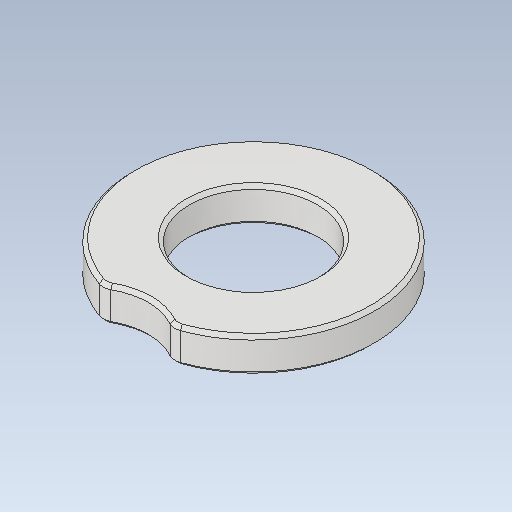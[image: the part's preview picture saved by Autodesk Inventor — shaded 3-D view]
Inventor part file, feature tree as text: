
AUTODESK INVENTOR PART (.ipt)
format: ipt  version: 2020.1 (Build 241239000, 239)  size: 160,256 bytes
history: native  units: mm
features: chamfer x2, extrude x1, fillet x1, sketch x1
ambient origin geometry x8: Origin, YZ Plane, XZ Plane, XY Plane, X Axis, Y Axis, Z Axis, Center Point
bodies: Solid1 (feature_tree)
feature tree (5):
  extrude  "Extrusion1"  Depth=10.0mm
  fillet  "Fillet1"  Radius=40.0mm
  chamfer  "Chamfer1"  Angle=45.0deg  [1 undecoded]
  chamfer  "Chamfer2"  Distance=20.0mm
  sketch  "Sketch1"  dims[d0=18.5mm d2=3.4mm d4=40.0mm d6=360.0deg d8=45.0deg d10=20.0mm d11=10.0mm d12=5.0mm d13=0.0mm d14=2.0mm d24=0.5mm d25=2.0mm d26=45.0deg d30=7.5mm d31=3.75mm d32=0.5mm d33=2.0mm d34=45.0deg]
note: 1 required parameter value undecoded (feature->parameter linkage not recoverable at this tier; creation-order binding heuristic only, values carry confidence <= 0.55)
